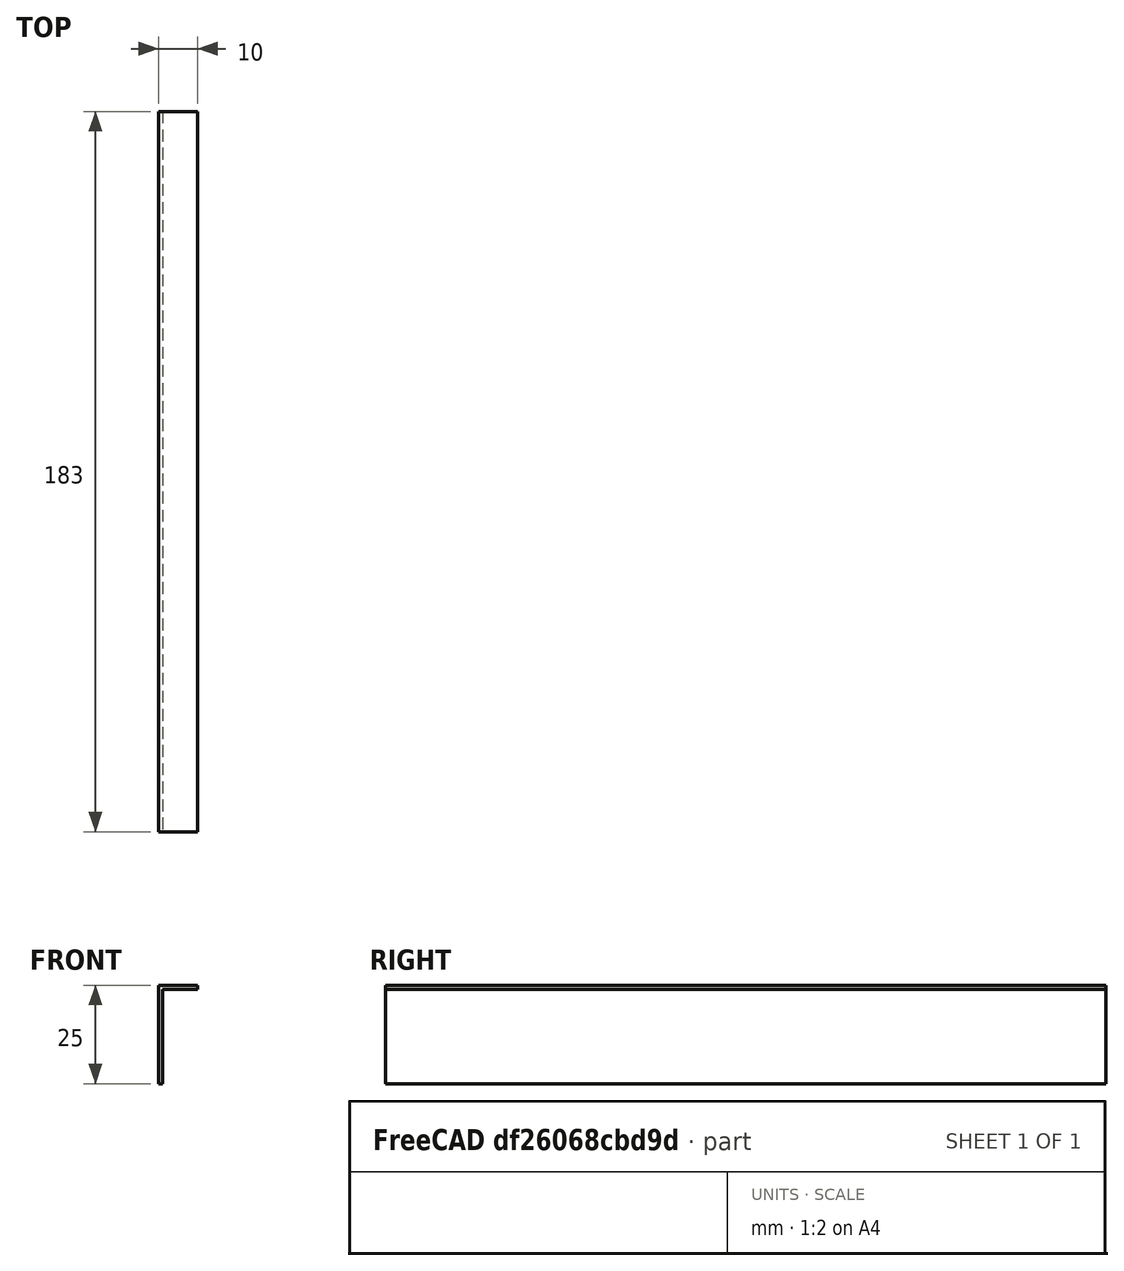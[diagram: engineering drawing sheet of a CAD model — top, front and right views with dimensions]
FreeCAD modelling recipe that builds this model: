
FCSTD DOCUMENT  (FreeCAD 0.21R33694 (Git))
Label: baguette-info-tirettes-ub
License: Creative Commons Attribution 3.0
LicenseURL: http://en.wikipedia.org/wiki/Public_domain
objects: Sketcher::SketchObject×1, PartDesign::Pad×1, PartDesign::Body×1
note: 4 computed .brp shape members not serialized (recipe doc carries the construction recipe); baked Part::Feature solids carry a one-line shape summary decoded from their .brp

FEATURE [Sketcher::SketchObject] Sketch
  FullyConstrained = true
  MapMode = 5
  Placement = pos=(0,0,0) rot=(1,0,0;1.5708rad)
  Support = -> [XZ_Plane]
  sketch-geometry (6):
    g0: LineSegment StartX=9 StartY=0 StartZ=0 EndX=0 EndY=0 EndZ=0
    g1: LineSegment StartX=0 StartY=0 StartZ=0 EndX=0 EndY=-24 EndZ=0
    g2: LineSegment StartX=0 StartY=-24 StartZ=0 EndX=-1 EndY=-24 EndZ=0
    g3: LineSegment StartX=-1 StartY=-24 StartZ=0 EndX=-1 EndY=1 EndZ=0
    g4: LineSegment StartX=-1 StartY=1 StartZ=0 EndX=9 EndY=1 EndZ=0
    g5: LineSegment StartX=9 StartY=1 StartZ=0 EndX=9 EndY=0 EndZ=0
  constraints (17):
    c: PointOnObject(g0,g-1)
    c: Coincident(g0,g-1)
    c: Coincident(g0,g1)
    c: PointOnObject(g1,g-2)
    c: Coincident(g1,g2)
    c: Horizontal(g2)
    c: Coincident(g2,g3)
    c: Vertical(g3)
    c: Coincident(g3,g4)
    c: Horizontal(g4)
    c: Coincident(g4,g5)
    c: Coincident(g5,g0)
    c: Vertical(g5)
    c: DistanceY(g5,g5) = 1
    c: DistanceX(g2,g2) = 1
    c: DistanceX(g4,g4) = 10
    c: DistanceY(g3,g3) = 25
FEATURE [PartDesign::Pad] Pad
  Direction = (0,-1,-2e-16)
  Length = 183
  Length2 = 10
  Placement = pos=(0,0,0) rot=(1,0,0;1.5708rad)
  Profile = -> Sketch
  ReferenceAxis = -> Sketch [N_Axis]
  Type = 0
FEATURE [PartDesign::Body] Body
  Group = -> [Sketch,Pad]
  Origin = -> Origin
  Tip = -> Pad
